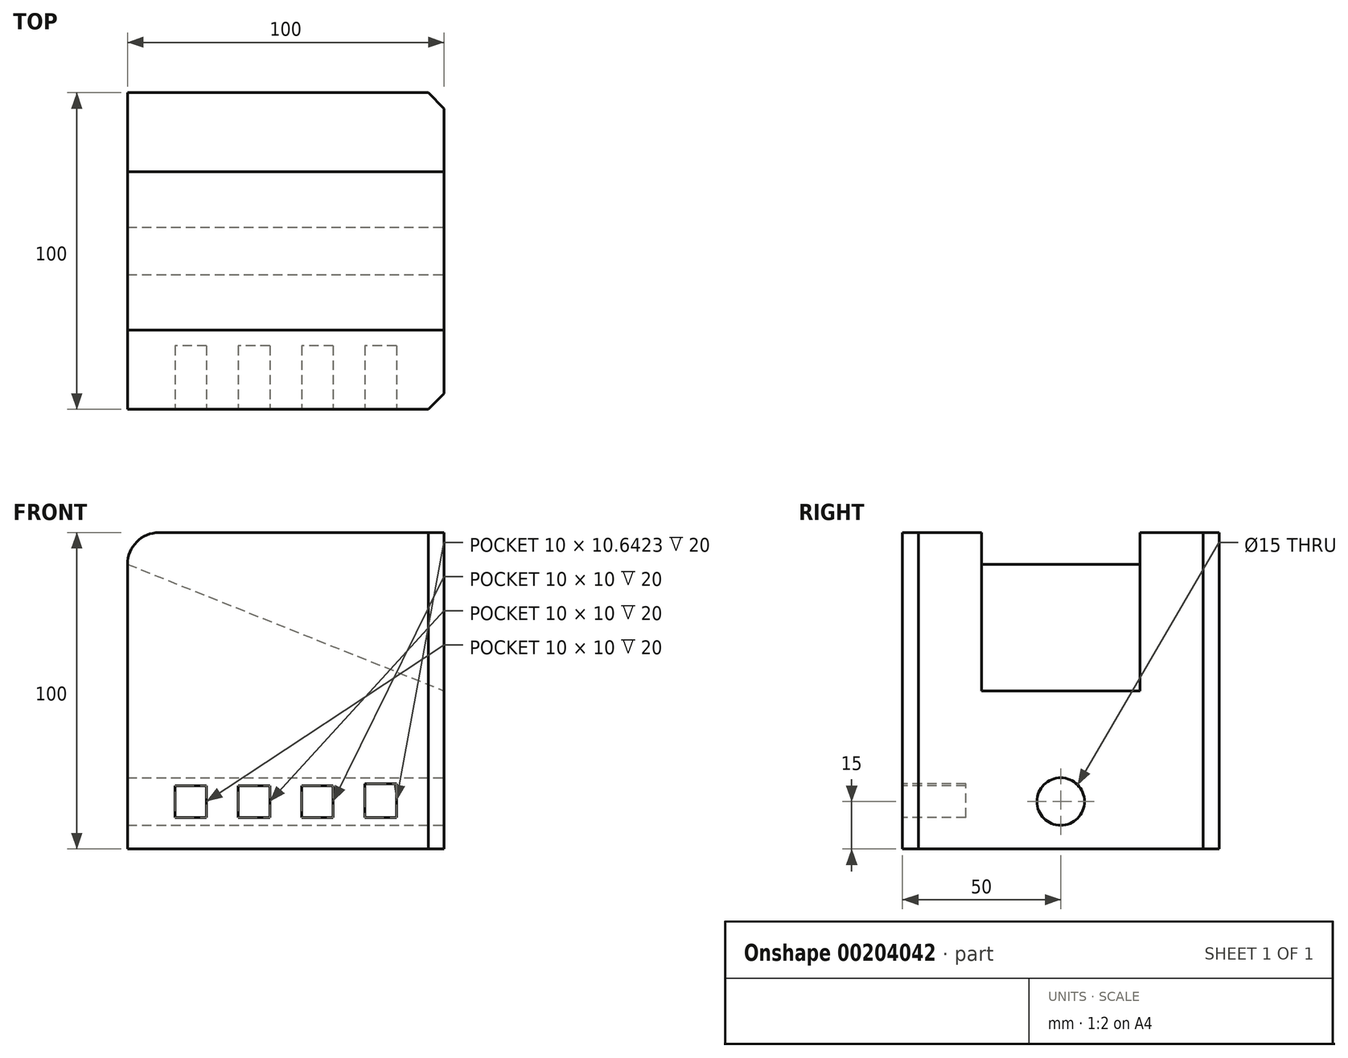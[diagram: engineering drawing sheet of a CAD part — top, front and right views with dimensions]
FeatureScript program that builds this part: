
annotation { "Feature Type Name" : "Feature", "Feature Type Description" : "" }
export const myFeature = defineFeature(function(context is Context, id is Id, definition is map)
    precondition{}
    {
        {
            var Q0;
            Q0=qCreatedBy(makeId("Right.planeOp"),FACE);
            var sketch = newSketch(context, id + "F0", { "sketchPlane" : qUnion([Q0])});
            skLineSegment(sketch, "E0", {"start": v(0, 0) * mm, "end": v(0, 100) * mm});
            skLineSegment(sketch, "E1", {"start": v(100, 100) * mm, "end": v(100, 0) * mm});
            skLineSegment(sketch, "E2", {"start": v(0, 0) * mm, "end": v(100, 0) * mm});
            skLineSegment(sketch, "E3", {"start": v(0, 100) * mm, "end": v(25, 100) * mm});
            skLineSegment(sketch, "E4", {"start": v(0, 0) * mm, "end": v(50, 0) * mm});
            skLineSegment(sketch, "E5", {"start": v(50, 0) * mm, "end": v(50, 15) * mm});
            skLineSegment(sketch, "E6", {"start": v(25, 100) * mm, "end": v(25, 50) * mm});
            skLineSegment(sketch, "E7", {"start": v(25, 50) * mm, "end": v(75, 50) * mm});
            skLineSegment(sketch, "E8", {"start": v(75, 50) * mm, "end": v(75, 100) * mm});
            skLineSegment(sketch, "E9", {"start": v(25, 100) * mm, "end": v(25, 90) * mm});
            skLineSegment(sketch, "E10", {"start": v(25, 90) * mm, "end": v(75, 90) * mm});
            skLineSegment(sketch, "E11", {"start": v(75, 100) * mm, "end": v(100, 100) * mm});
            skLineSegment(sketch, "E12", {"start": v(0, 0) * mm, "end": v(5, 0) * mm});
            skLineSegment(sketch, "E13", {"start": v(5, 0) * mm, "end": v(5, 100) * mm});
            skLineSegment(sketch, "E14", {"start": v(100, 0) * mm, "end": v(95, 0) * mm});
            skLineSegment(sketch, "E15", {"start": v(95, 0) * mm, "end": v(95, 100) * mm});
            skCircle(sketch, "E16", {"center": v(50, 15) * mm, "radius": 7.5 * mm});
            skSolve(sketch);
        }
        {
            var Q0;
            Q0 = qSketchRegion(id + "F0", true);
            extrude(context, id + "F1", {"entities" : qUnion([Q0]), "oppositeDirection" : true, "depth" : 100 * mm});
        }
        {
            var Q0;
            Q0=qCreatedBy(makeId("Front.planeOp"),FACE);
            var sketch = newSketch(context, id + "F2", { "sketchPlane" : qUnion([Q0])});
            skLineSegment(sketch, "E17", {"start": v(0, 0) * mm, "end": v(-5, 0) * mm});
            skLineSegment(sketch, "E18", {"start": v(-5, 0) * mm, "end": v(-5, 100) * mm});
            skLineSegment(sketch, "E19", {"start": v(0, 0) * mm, "end": v(-15, 0) * mm});
            skPoint(sketch, "E19.endSnap0", {"position": v(-2.5, 0) * mm});
            skLineSegment(sketch, "E20.bottom", {"start": v(-15, 10) * mm, "end": v(-25, 10) * mm});
            skLineSegment(sketch, "E20.top", {"start": v(-15, 20.64) * mm, "end": v(-25, 20.64) * mm});
            skLineSegment(sketch, "E20.left", {"start": v(-15, 10) * mm, "end": v(-15, 20.64) * mm});
            skLineSegment(sketch, "E20.right", {"start": v(-25, 10) * mm, "end": v(-25, 20.64) * mm});
            skLineSegment(sketch, "E21.bottom", {"start": v(-35, 10) * mm, "end": v(-45, 10) * mm});
            skLineSegment(sketch, "E21.top", {"start": v(-35, 20) * mm, "end": v(-45, 20) * mm});
            skLineSegment(sketch, "E21.left", {"start": v(-35, 10) * mm, "end": v(-35, 20) * mm});
            skLineSegment(sketch, "E21.right", {"start": v(-45, 10) * mm, "end": v(-45, 20) * mm});
            skLineSegment(sketch, "E22.bottom", {"start": v(-55, 10) * mm, "end": v(-65, 10) * mm});
            skLineSegment(sketch, "E22.top", {"start": v(-55, 20) * mm, "end": v(-65, 20) * mm});
            skLineSegment(sketch, "E22.left", {"start": v(-55, 10) * mm, "end": v(-55, 20) * mm});
            skLineSegment(sketch, "E22.right", {"start": v(-65, 10) * mm, "end": v(-65, 20) * mm});
            skLineSegment(sketch, "E23.bottom", {"start": v(-75, 10) * mm, "end": v(-85, 10) * mm});
            skLineSegment(sketch, "E23.top", {"start": v(-75, 20) * mm, "end": v(-85, 20) * mm});
            skLineSegment(sketch, "E23.left", {"start": v(-75, 10) * mm, "end": v(-75, 20) * mm});
            skLineSegment(sketch, "E23.right", {"start": v(-85, 10) * mm, "end": v(-85, 20) * mm});
            skLineSegment(sketch, "E24", {"start": v(-15, 0) * mm, "end": v(-100, 0) * mm});
            skSolve(sketch);
        }
        {
            var Q0;
            Q0=makeQuery(id+"F2.imprint","IMPRINT",FACE,{"disambiguationData":[TD([[makeQuery(id+"F2.imprint","IMPRINT",EDGE,{"derivedFrom":sQuery(id+"F2.wireOp",EDGE,"E23.bottom")}),-1.0]])]});
            var Q1;
            Q1=makeQuery(id+"F2.imprint","IMPRINT",FACE,{"disambiguationData":[TD([[makeQuery(id+"F2.imprint","IMPRINT",EDGE,{"derivedFrom":sQuery(id+"F2.wireOp",EDGE,"E22.bottom")}),-1.0]])]});
            var Q2;
            Q2=makeQuery(id+"F2.imprint","IMPRINT",FACE,{"disambiguationData":[TD([[makeQuery(id+"F2.imprint","IMPRINT",EDGE,{"derivedFrom":sQuery(id+"F2.wireOp",EDGE,"E21.bottom")}),-1.0]])]});
            var Q3;
            Q3=makeQuery(id+"F2.imprint","IMPRINT",FACE,{"disambiguationData":[TD([[makeQuery(id+"F2.imprint","IMPRINT",EDGE,{"derivedFrom":sQuery(id+"F2.wireOp",EDGE,"E20.bottom")}),-1.0]])]});
            extrude(context, id + "F3", {"entities" : qUnion([Q0, Q1, Q2, Q3]), "operationType" : NewBodyOperationType.REMOVE, "oppositeDirection" : true, "depth" : 20 * mm});
        }
        {
            var Q0;
            Q0=makeQuery(id+"F1.opExtrude","CAP_EDGE",EDGE,{"disambiguationData":[OSD([sQuery(id+"F0.wireOp",EDGE,"E3")])],"isStart":false});
            fillet(context, id + "F4", {"entities" : qUnion([Q0]), "radius" : 10 * mm, "tangentPropagation" : true, "allowEdgeOverflow" : false});
        }
        {
            var Q0;
            Q0=makeQuery(id+"F1.opExtrude","CAP_EDGE",EDGE,{"disambiguationData":[OSD([sQuery(id+"F0.wireOp",EDGE,"E11")])],"isStart":false});
            fillet(context, id + "F5", {"entities" : qUnion([Q0]), "radius" : 10 * mm, "tangentPropagation" : true, "allowEdgeOverflow" : false});
        }
        {
            var Q0;
            Q0=makeQuery(id+"F1.opExtrude","CAP_EDGE",EDGE,{"disambiguationData":[OSD([sQuery(id+"F0.wireOp",EDGE,"E0")])],"isStart":true});
            chamfer(context, id + "F6", {"entities" : qUnion([Q0]), "width" : 5 * mm, "tangentPropagation" : true});
        }
        {
            var Q0;
            Q0=makeQuery(id+"F1.opExtrude","CAP_EDGE",EDGE,{"disambiguationData":[OSD([sQuery(id+"F0.wireOp",EDGE,"E1")])],"isStart":true});
            chamfer(context, id + "F7", {"entities" : qUnion([Q0]), "width" : 5 * mm, "tangentPropagation" : true});
        }
        {
            var Q0;
            Q0=makeQuery(id+"F1.opExtrude","CAP_EDGE",EDGE,{"disambiguationData":[OSD([sQuery(id+"F0.wireOp",EDGE,"E10")])],"isStart":true});
            chamfer(context, id + "F8", {"entities" : qUnion([Q0]), "chamferType" : ChamferType.TWO_OFFSETS, "width1" : 100 * mm, "oppositeDirection" : false, "width2" : 40 * mm, "tangentPropagation" : true});
        }
        {
            var Q0;
            Q0=makeQuery(id+"F1.opExtrude","SWEPT_BODY",BODY,{"disambiguationData":[OSD([sQuery(id+"F0.wireOp",EDGE,"E0"),sQuery(id+"F0.wireOp",EDGE,"E1"),sQuery(id+"F0.wireOp",EDGE,"E2"),sQuery(id+"F0.wireOp",EDGE,"E3"),sQuery(id+"F0.wireOp",EDGE,"E4"),sQuery(id+"F0.wireOp",EDGE,"E8"),sQuery(id+"F0.wireOp",EDGE,"E9"),sQuery(id+"F0.wireOp",EDGE,"E10"),sQuery(id+"F0.wireOp",EDGE,"E11"),sQuery(id+"F0.wireOp",EDGE,"E12"),sQuery(id+"F0.wireOp",EDGE,"E14"),sQuery(id+"F0.wireOp",EDGE,"E16")])]});
            transform(context, id + "F9", {"entities" : qUnion([Q0]), "transformType" : TransformType.TRANSLATION_3D, "dx" : 100 * mm, "dy" : 0 * mm, "dz" : 0 * mm, "makeCopy" : false});
        }
    });
